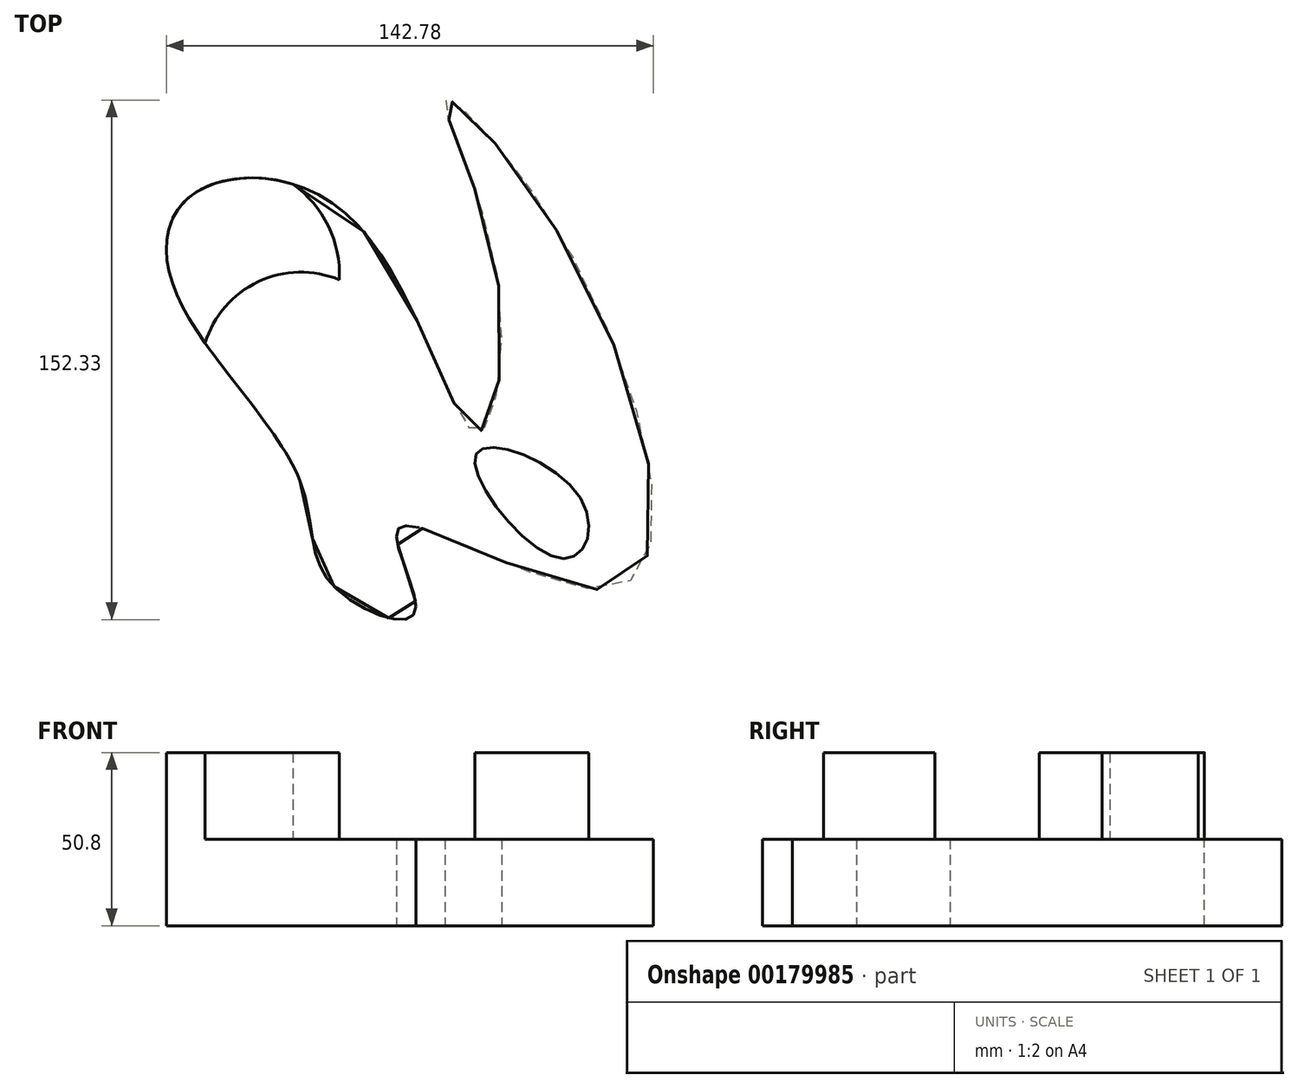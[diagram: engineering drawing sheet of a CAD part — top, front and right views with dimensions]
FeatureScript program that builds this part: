
annotation { "Feature Type Name" : "Feature", "Feature Type Description" : "" }
export const myFeature = defineFeature(function(context is Context, id is Id, definition is map)
    precondition{}
    {
        {
            var Q0;
            Q0=qCreatedBy(makeId("Top.planeOp"),FACE);
            var sketch = newSketch(context, id + "F0", { "sketchPlane" : qUnion([Q0])});
            skFitSpline(sketch, "E0", {"points": [v(-57.68, -31.77) * mm, v(-93.82, 22.87) * mm, v(-89.62, 51.83) * mm, v(-42.07, 44.59) * mm, v(-6.28, -17.4) * mm, v(0, 29.63) * mm, v(-14.88, 79.68) * mm, v(26.36, 25.93) * mm, v(34.48, -63.26) * mm, v(-28.73, -45.67) * mm, v(-24.07, -70.53) * mm, v(-48.34, -62.1) * mm, v(-57.68, -31.77) * mm]});
            skSolve(sketch);
        }
        {
            var Q0;
            Q0=makeQuery(id+"F0.imprint","IMPRINT",FACE,{"disambiguationData":[TD([[makeQuery(id+"F0.imprint","IMPRINT",EDGE,{"derivedFrom":sQuery(id+"F0.wireOp",EDGE,"E0")}),-1.0]])]});
            extrude(context, id + "F1", {"entities" : qUnion([Q0]), "depth" : 25.4 * mm});
        }
        {
            var Q0;
            Q0=makeQuery(id+"F1.opExtrude","CAP_FACE",FACE,{"disambiguationData":[OSD([sQuery(id+"F0.wireOp",EDGE,"E0")])],"isStart":false});
            var sketch = newSketch(context, id + "F2", { "sketchPlane" : qUnion([Q0])});
            skCircle(sketch, "E1", {"center": v(-78.81, 28.7) * mm, "radius": 32.7 * mm});
            skCircle(sketch, "E2", {"center": v(-57.4, 0) * mm, "radius": 29.43 * mm});
            skCircle(sketch, "E3", {"center": v(-33.28, -30.73) * mm, "radius": 20.7 * mm});
            skSolve(sketch);
        }
        {
            var Q0;
            {var subQ0=sQuery(id+"F2.wireOp",EDGE,"E2");var subQ1=sQuery(id+"F2.wireOp",EDGE,"E1");var subQ2=makeQuery(id+"F2.imprint","INTERSECT",VERTEX,{"disambiguationData":[OD(1.0)],"derivedFrom":[subQ1,subQ0]});Q0=makeQuery(id+"F2.imprint","IMPRINT",FACE,{"disambiguationData":[TD([[makeQuery(id+"F2.imprint","IMPRINT",EDGE,{"disambiguationData":[TD([[subQ2,-1.0]])],"derivedFrom":subQ1}),1.0]])]});}
            extrude(context, id + "F3", {"entities" : qUnion([Q0]), "operationType" : NewBodyOperationType.ADD, "depth" : 25.4 * mm});
        }
        {
            var Q0;
            Q0=makeQuery(id+"F1.opExtrude","CAP_FACE",FACE,{"disambiguationData":[OSD([sQuery(id+"F0.wireOp",EDGE,"E0")])],"isStart":false});
            var sketch = newSketch(context, id + "F4", { "sketchPlane" : qUnion([Q0])});
            skFitSpline(sketch, "E4", {"points": [v(-56.99, -15.54) * mm, v(-34.24, -48.59) * mm, v(-48.99, -40.31) * mm, v(-56.99, -15.54) * mm]});
            skFitSpline(sketch, "E5", {"points": [v(-5.99, -23.88) * mm, v(19.07, -54.55) * mm, v(24.97, -37.5) * mm, v(-5.99, -23.88) * mm]});
            skSolve(sketch);
        }
        {
            var Q0;
            Q0=makeQuery(id+"F4.imprint","IMPRINT",FACE,{"disambiguationData":[TD([[makeQuery(id+"F4.imprint","IMPRINT",EDGE,{"derivedFrom":sQuery(id+"F4.wireOp",EDGE,"E5")}),1.0]])]});
            extrude(context, id + "F5", {"entities" : qUnion([Q0]), "operationType" : NewBodyOperationType.ADD, "depth" : 25.4 * mm});
        }
    });
